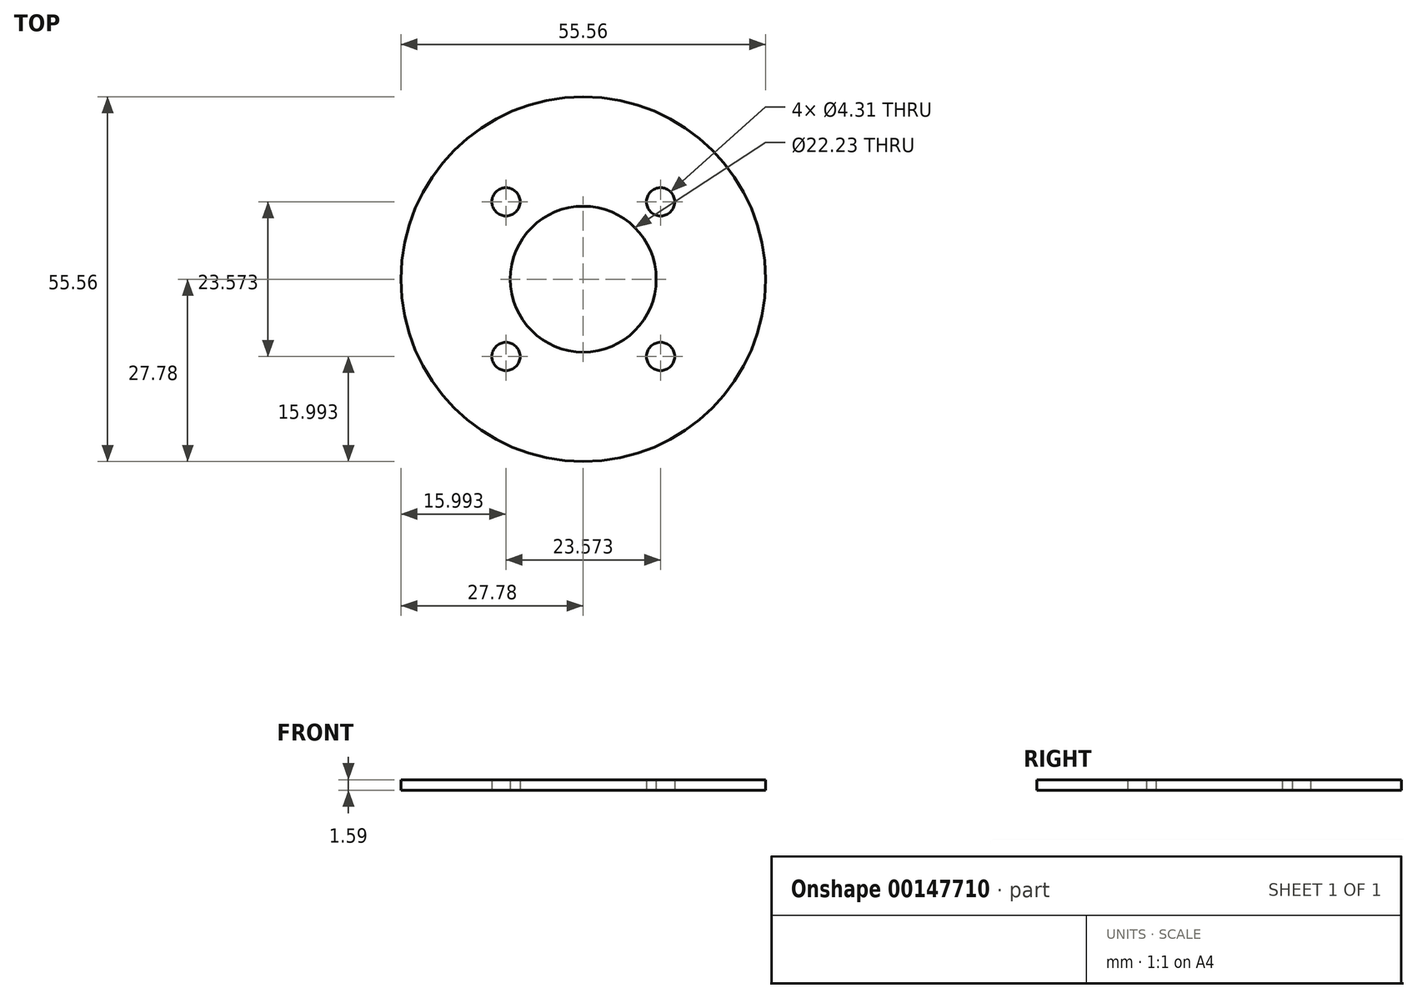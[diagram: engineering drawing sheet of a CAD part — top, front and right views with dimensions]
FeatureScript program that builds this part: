
annotation { "Feature Type Name" : "Feature", "Feature Type Description" : "" }
export const myFeature = defineFeature(function(context is Context, id is Id, definition is map)
    precondition{}
    {
        {
            var Q0;
            Q0=qCreatedBy(makeId("Top.planeOp"),FACE);
            var sketch = newSketch(context, id + "F0", { "sketchPlane" : qUnion([Q0])});
            skCircle(sketch, "E0", {"center": v(0, 0) * mm, "radius": 27.78 * mm});
            skLineSegment(sketch, "E1.bottom", {"start": v(-11.79, 11.79) * mm, "end": v(11.79, 11.79) * mm, "construction": true});
            skLineSegment(sketch, "E1.top", {"start": v(-11.79, -11.79) * mm, "end": v(11.79, -11.79) * mm, "construction": true});
            skLineSegment(sketch, "E1.left", {"start": v(-11.79, 11.79) * mm, "end": v(-11.79, -11.79) * mm, "construction": true});
            skLineSegment(sketch, "E1.right", {"start": v(11.79, 11.79) * mm, "end": v(11.79, -11.79) * mm, "construction": true});
            skCircle(sketch, "E2", {"center": v(-11.79, 11.79) * mm, "radius": 5.56 * mm, "construction": true});
            skCircle(sketch, "E3", {"center": v(11.79, 11.79) * mm, "radius": 3.97 * mm, "construction": true});
            skCircle(sketch, "E4", {"center": v(-11.79, 11.79) * mm, "radius": 2.15 * mm});
            skCircle(sketch, "E5", {"center": v(-11.79, -11.79) * mm, "radius": 3.97 * mm, "construction": true});
            skCircle(sketch, "E6", {"center": v(11.79, -11.79) * mm, "radius": 2.15 * mm});
            skCircle(sketch, "E7", {"center": v(0, 0) * mm, "radius": 11.11 * mm});
            skCircle(sketch, "E8", {"center": v(-11.79, -11.79) * mm, "radius": 2.15 * mm});
            skCircle(sketch, "E9", {"center": v(11.79, 11.79) * mm, "radius": 2.15 * mm});
            skSolve(sketch);
        }
        {
            var Q0;
            Q0=qSketchRegion(id+"F0",true);
            extrude(context, id + "F1", {"entities" : qUnion([Q0]), "depth" : 1.59 * mm});
        }
    });
